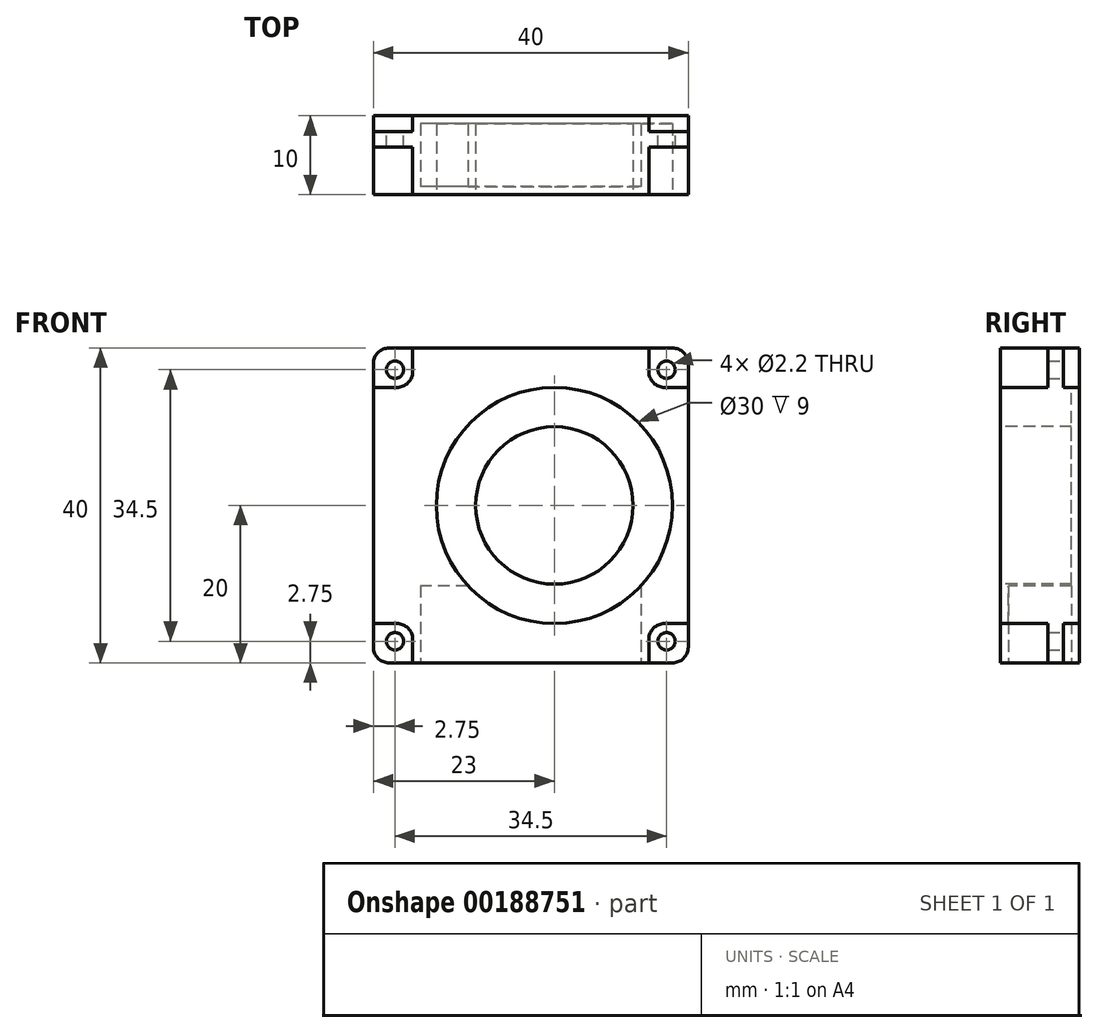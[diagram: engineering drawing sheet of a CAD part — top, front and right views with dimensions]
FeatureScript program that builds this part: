
annotation { "Feature Type Name" : "Feature", "Feature Type Description" : "" }
export const myFeature = defineFeature(function(context is Context, id is Id, definition is map)
    precondition{}
    {
        {
            var Q0;
            Q0=qCreatedBy(makeId("Front.planeOp"),FACE);
            var sketch = newSketch(context, id + "F0", { "sketchPlane" : qUnion([Q0])});
            skLineSegment(sketch, "E0.bottom", {"start": v(18, -20) * mm, "end": v(-18, -20) * mm});
            skLineSegment(sketch, "E0.top", {"start": v(18, 20) * mm, "end": v(-18, 20) * mm});
            skLineSegment(sketch, "E0.left", {"start": v(20, -18) * mm, "end": v(20, 18) * mm});
            skLineSegment(sketch, "E0.right", {"start": v(-20, -18) * mm, "end": v(-20, 18) * mm});
            skPoint(sketch, "E0.middle", {"position": v(0, 0) * mm});
            skCircle(sketch, "E1", {"center": v(-17.25, 17.25) * mm, "radius": 1.1 * mm});
            skLineSegment(sketch, "E2", {"start": v(-20, 20) * mm, "end": v(20, -20) * mm, "construction": true});
            skCircle(sketch, "E3.1.0", {"center": v(-17.25, -17.25) * mm, "radius": 1.1 * mm});
            skCircle(sketch, "E3.2.0", {"center": v(17.25, -17.25) * mm, "radius": 1.1 * mm});
            skCircle(sketch, "E3.3.0", {"center": v(17.25, 17.25) * mm, "radius": 1.1 * mm});
            skLineSegment(sketch, "E4", {"start": v(0, 0) * mm, "end": v(0, 20) * mm, "construction": true});
            skPoint(sketch, "E5.visualSharp", {"position": v(-20, 20) * mm});
            skArc(sketch, "E5.filletArc", {"start": v(-18, 20) * mm, "mid": v(-19.41, 19.41) * mm, "end": v(-20, 18) * mm});
            skPoint(sketch, "E6.visualSharp", {"position": v(20, 20) * mm});
            skArc(sketch, "E6.filletArc", {"start": v(20, 18) * mm, "mid": v(19.41, 19.41) * mm, "end": v(18, 20) * mm});
            skPoint(sketch, "E7.visualSharp", {"position": v(20, -20) * mm});
            skArc(sketch, "E7.filletArc", {"start": v(18, -20) * mm, "mid": v(19.41, -19.41) * mm, "end": v(20, -18) * mm});
            skPoint(sketch, "E8.visualSharp", {"position": v(-20, -20) * mm});
            skArc(sketch, "E8.filletArc", {"start": v(-20, -18) * mm, "mid": v(-19.41, -19.41) * mm, "end": v(-18, -20) * mm});
            skSolve(sketch);
        }
        {
            var Q0;
            Q0=makeQuery(id+"F0.imprint","IMPRINT",FACE,{"disambiguationData":[TD([[makeQuery(id+"F0.imprint","IMPRINT",EDGE,{"derivedFrom":sQuery(id+"F0.wireOp",EDGE,"E0.bottom")}),-1.0]])]});
            extrude(context, id + "F1", {"entities" : qUnion([Q0]), "depth" : 10 * mm, "offsetDistance" : 25 * mm});
        }
        {
            var Q0;
            Q0=makeQuery(id+"F1.opExtrude","CAP_FACE",FACE,{"disambiguationData":[OSD([sQuery(id+"F0.wireOp",EDGE,"E0.bottom"),sQuery(id+"F0.wireOp",EDGE,"E0.top"),sQuery(id+"F0.wireOp",EDGE,"E0.left"),sQuery(id+"F0.wireOp",EDGE,"E0.right"),sQuery(id+"F0.wireOp",EDGE,"E1"),sQuery(id+"F0.wireOp",EDGE,"E3.1.0"),sQuery(id+"F0.wireOp",EDGE,"E3.2.0"),sQuery(id+"F0.wireOp",EDGE,"E3.3.0"),sQuery(id+"F0.wireOp",EDGE,"E5.filletArc"),sQuery(id+"F0.wireOp",EDGE,"E6.filletArc"),sQuery(id+"F0.wireOp",EDGE,"E7.filletArc"),sQuery(id+"F0.wireOp",EDGE,"E8.filletArc")])],"isStart":false});
            var sketch = newSketch(context, id + "F2", { "sketchPlane" : qUnion([Q0])});
            skLineSegment(sketch, "E9", {"start": v(-15, -20) * mm, "end": v(-15, -17) * mm});
            skLineSegment(sketch, "E10", {"start": v(0, 0) * mm, "end": v(0, -20) * mm, "construction": true});
            skLineSegment(sketch, "E11", {"start": v(0, 0) * mm, "end": v(-20, 0) * mm, "construction": true});
            skLineSegment(sketch, "E12", {"start": v(-20, -15) * mm, "end": v(-17, -15) * mm});
            skArc(sketch, "E13", {"start": v(-15, -17) * mm, "mid": v(-15.59, -15.59) * mm, "end": v(-17, -15) * mm});
            skLineSegment(sketch, "E14.MirrorCS", {"start": v(20, -15) * mm, "end": v(17, -15) * mm});
            skLineSegment(sketch, "E15.MirrorCS", {"start": v(15, -20) * mm, "end": v(15, -17) * mm});
            skArc(sketch, "E16.MirrorCS", {"start": v(15, -17) * mm, "mid": v(15.59, -15.59) * mm, "end": v(17, -15) * mm});
            skLineSegment(sketch, "E17.MirrorCS", {"start": v(20, 15) * mm, "end": v(17, 15) * mm});
            skLineSegment(sketch, "E18.MirrorCS", {"start": v(-15, 20) * mm, "end": v(-15, 17) * mm});
            skLineSegment(sketch, "E19.MirrorCS", {"start": v(-20, 15) * mm, "end": v(-17, 15) * mm});
            skLineSegment(sketch, "E20.MirrorCS", {"start": v(15, 20) * mm, "end": v(15, 17) * mm});
            skArc(sketch, "E21.MirrorCS", {"start": v(-15, 17) * mm, "mid": v(-15.59, 15.59) * mm, "end": v(-17, 15) * mm});
            skArc(sketch, "E22.MirrorCS", {"start": v(15, 17) * mm, "mid": v(15.59, 15.59) * mm, "end": v(17, 15) * mm});
            skSolve(sketch);
        }
        {
            var Q0;
            {var subQ1=sQuery(id+"F2.wireOp",EDGE,"E9");Q0=makeQuery(id+"F2.imprint","IMPRINT",FACE,{"disambiguationData":[TD([[makeQuery(id+"F2.imprint","IMPRINT",EDGE,{"derivedFrom":subQ1}),1.0]])]});}
            var Q1;
            {var subQ3=sQuery(id+"F2.wireOp",EDGE,"E18.MirrorCS");Q1=makeQuery(id+"F2.imprint","IMPRINT",FACE,{"disambiguationData":[TD([[makeQuery(id+"F2.imprint","IMPRINT",EDGE,{"derivedFrom":subQ3}),-1.0]])]});}
            var Q2;
            {var subQ1=sQuery(id+"F2.wireOp",EDGE,"E17.MirrorCS");Q2=makeQuery(id+"F2.imprint","IMPRINT",FACE,{"disambiguationData":[TD([[makeQuery(id+"F2.imprint","IMPRINT",EDGE,{"derivedFrom":subQ1}),-1.0]])]});}
            var Q3;
            {var subQ0=sQuery(id+"F2.wireOp",EDGE,"E14.MirrorCS");Q3=makeQuery(id+"F2.imprint","IMPRINT",FACE,{"disambiguationData":[TD([[makeQuery(id+"F2.imprint","IMPRINT",EDGE,{"derivedFrom":subQ0}),1.0]])]});}
            extrude(context, id + "F3", {"entities" : qUnion([Q0, Q1, Q2, Q3]), "operationType" : NewBodyOperationType.REMOVE, "oppositeDirection" : true, "depth" : 6 * mm, "offsetDistance" : 25 * mm});
        }
        {
            var Q0;
            Q0=makeQuery(id+"F1.opExtrude","CAP_FACE",FACE,{"disambiguationData":[OSD([sQuery(id+"F0.wireOp",EDGE,"E0.bottom"),sQuery(id+"F0.wireOp",EDGE,"E0.top"),sQuery(id+"F0.wireOp",EDGE,"E0.left"),sQuery(id+"F0.wireOp",EDGE,"E0.right"),sQuery(id+"F0.wireOp",EDGE,"E1"),sQuery(id+"F0.wireOp",EDGE,"E3.1.0"),sQuery(id+"F0.wireOp",EDGE,"E3.2.0"),sQuery(id+"F0.wireOp",EDGE,"E3.3.0"),sQuery(id+"F0.wireOp",EDGE,"E5.filletArc"),sQuery(id+"F0.wireOp",EDGE,"E6.filletArc"),sQuery(id+"F0.wireOp",EDGE,"E7.filletArc"),sQuery(id+"F0.wireOp",EDGE,"E8.filletArc")])],"isStart":true});
            var sketch = newSketch(context, id + "F4", { "sketchPlane" : qUnion([Q0])});
            skLineSegment(sketch, "E23.0.0", {"start": v(17, -15) * mm, "end": v(20, -15) * mm});
            skLineSegment(sketch, "E23.0.1", {"start": v(20, -15) * mm, "end": v(20, -18) * mm});
            skArc(sketch, "E23.0.2", {"start": v(20, -18) * mm, "mid": v(19.41, -19.41) * mm, "end": v(18, -20) * mm});
            skLineSegment(sketch, "E23.0.3", {"start": v(18, -20) * mm, "end": v(15, -20) * mm});
            skLineSegment(sketch, "E23.0.4", {"start": v(15, -20) * mm, "end": v(15, -17) * mm});
            skArc(sketch, "E23.0.5", {"start": v(15, -17) * mm, "mid": v(15.59, -15.59) * mm, "end": v(17, -15) * mm});
            skLineSegment(sketch, "E24.0.0", {"start": v(-15, -17) * mm, "end": v(-15, -20) * mm});
            skLineSegment(sketch, "E24.0.1", {"start": v(-15, -20) * mm, "end": v(-18, -20) * mm});
            skArc(sketch, "E24.0.2", {"start": v(-18, -20) * mm, "mid": v(-19.41, -19.41) * mm, "end": v(-20, -18) * mm});
            skLineSegment(sketch, "E24.0.3", {"start": v(-20, -18) * mm, "end": v(-20, -15) * mm});
            skLineSegment(sketch, "E24.0.4", {"start": v(-20, -15) * mm, "end": v(-17, -15) * mm});
            skArc(sketch, "E24.0.5", {"start": v(-17, -15) * mm, "mid": v(-15.59, -15.59) * mm, "end": v(-15, -17) * mm});
            skLineSegment(sketch, "E25.0.0", {"start": v(-18, 20) * mm, "end": v(-15, 20) * mm});
            skLineSegment(sketch, "E25.0.1", {"start": v(-15, 20) * mm, "end": v(-15, 17) * mm});
            skArc(sketch, "E25.0.2", {"start": v(-15, 17) * mm, "mid": v(-15.59, 15.59) * mm, "end": v(-17, 15) * mm});
            skLineSegment(sketch, "E25.0.3", {"start": v(-17, 15) * mm, "end": v(-20, 15) * mm});
            skLineSegment(sketch, "E25.0.4", {"start": v(-20, 15) * mm, "end": v(-20, 18) * mm});
            skArc(sketch, "E25.0.5", {"start": v(-20, 18) * mm, "mid": v(-19.41, 19.41) * mm, "end": v(-18, 20) * mm});
            skLineSegment(sketch, "E26.0.0", {"start": v(20, 18) * mm, "end": v(20, 15) * mm});
            skLineSegment(sketch, "E26.0.1", {"start": v(20, 15) * mm, "end": v(17, 15) * mm});
            skArc(sketch, "E26.0.2", {"start": v(17, 15) * mm, "mid": v(15.59, 15.59) * mm, "end": v(15, 17) * mm});
            skLineSegment(sketch, "E26.0.3", {"start": v(15, 17) * mm, "end": v(15, 20) * mm});
            skLineSegment(sketch, "E26.0.4", {"start": v(15, 20) * mm, "end": v(18, 20) * mm});
            skArc(sketch, "E26.0.5", {"start": v(18, 20) * mm, "mid": v(19.41, 19.41) * mm, "end": v(20, 18) * mm});
            skSolve(sketch);
        }
        {
            var Q0;
            Q0=makeQuery(id+"F4.imprint","IMPRINT",FACE,{"disambiguationData":[TD([[makeQuery(id+"F4.imprint","IMPRINT",EDGE,{"derivedFrom":sQuery(id+"F4.wireOp",EDGE,"E24.0.0")}),-1.0]])]});
            var Q1;
            Q1=makeQuery(id+"F4.imprint","IMPRINT",FACE,{"disambiguationData":[TD([[makeQuery(id+"F4.imprint","IMPRINT",EDGE,{"derivedFrom":sQuery(id+"F4.wireOp",EDGE,"E25.0.0")}),-1.0]])]});
            var Q2;
            Q2=makeQuery(id+"F4.imprint","IMPRINT",FACE,{"disambiguationData":[TD([[makeQuery(id+"F4.imprint","IMPRINT",EDGE,{"derivedFrom":sQuery(id+"F4.wireOp",EDGE,"E26.0.0")}),1.0]])]});
            var Q3;
            Q3=makeQuery(id+"F4.imprint","IMPRINT",FACE,{"disambiguationData":[TD([[makeQuery(id+"F4.imprint","IMPRINT",EDGE,{"derivedFrom":sQuery(id+"F4.wireOp",EDGE,"E23.0.0")}),-1.0]])]});
            extrude(context, id + "F5", {"entities" : qUnion([Q0, Q1, Q2, Q3]), "operationType" : NewBodyOperationType.REMOVE, "oppositeDirection" : true, "depth" : 2 * mm, "offsetDistance" : 25 * mm});
        }
        {
            var Q0;
            {var subQ9=sQuery(id+"F2.wireOp",EDGE,"E9");Q0=makeQuery(id+"F2.imprint","IMPRINT",FACE,{"disambiguationData":[TD([[makeQuery(id+"F2.imprint","IMPRINT",EDGE,{"derivedFrom":subQ9}),-1.0]])]});}
            var sketch = newSketch(context, id + "F6", { "sketchPlane" : qUnion([Q0])});
            skCircle(sketch, "E27", {"center": v(3, 0) * mm, "radius": 15 * mm});
            skCircle(sketch, "E28", {"center": v(3, 0) * mm, "radius": 10 * mm});
            skSolve(sketch);
        }
        {
            var Q0;
            Q0=makeQuery(id+"F6.imprint","IMPRINT",FACE,{"disambiguationData":[TD([[makeQuery(id+"F6.imprint","IMPRINT",EDGE,{"derivedFrom":sQuery(id+"F6.wireOp",EDGE,"E27")}),1.0]])]});
            extrude(context, id + "F7", {"entities" : qUnion([Q0]), "operationType" : NewBodyOperationType.REMOVE, "oppositeDirection" : true, "depth" : 9 * mm, "offsetDistance" : 25 * mm});
        }
        {
            var Q0;
            Q0=makeQuery(id+"F1.opExtrude","SWEPT_FACE",FACE,{"disambiguationData":[OSD([sQuery(id+"F0.wireOp",EDGE,"E0.bottom")])]});
            var sketch = newSketch(context, id + "F8", { "sketchPlane" : qUnion([Q0])});
            skLineSegment(sketch, "E29.bottom", {"start": v(14, 1) * mm, "end": v(-14, 1) * mm});
            skLineSegment(sketch, "E29.top", {"start": v(14, 9) * mm, "end": v(-14, 9) * mm});
            skLineSegment(sketch, "E29.left", {"start": v(14, 1) * mm, "end": v(14, 9) * mm});
            skLineSegment(sketch, "E29.right", {"start": v(-14, 1) * mm, "end": v(-14, 9) * mm});
            skPoint(sketch, "E29.middle", {"position": v(0, 5) * mm});
            skPoint(sketch, "E29.middle.positionSnap0", {"position": v(0, 10) * mm});
            skPoint(sketch, "E29.centerSnap0", {"position": v(0, 10) * mm});
            skSolve(sketch);
        }
        {
            var Q0;
            Q0=makeQuery(id+"F8.imprint","IMPRINT",FACE,{"disambiguationData":[TD([[makeQuery(id+"F8.imprint","IMPRINT",EDGE,{"derivedFrom":sQuery(id+"F8.wireOp",EDGE,"E29.bottom")}),-1.0]])]});
            extrude(context, id + "F9", {"entities" : qUnion([Q0]), "operationType" : NewBodyOperationType.REMOVE, "oppositeDirection" : true, "depth" : 9.8 * mm, "offsetDistance" : 25 * mm});
        }
    });
